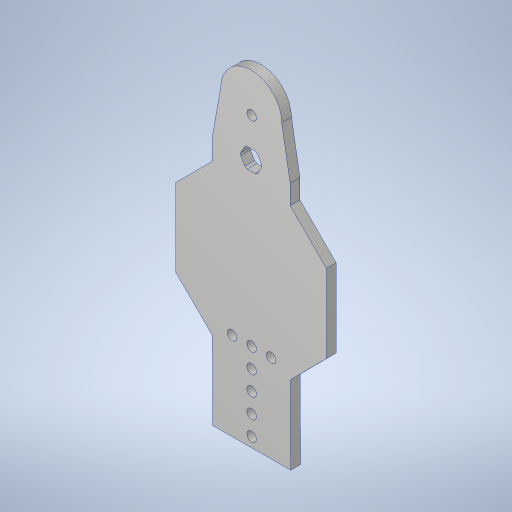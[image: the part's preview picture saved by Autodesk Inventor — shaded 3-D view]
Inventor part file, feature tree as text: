
AUTODESK INVENTOR PART (.ipt)
format: ipt  version: 2023.4 (Build 274418000, 418)  size: 311,808 bytes
history: native  units: in
note: dims shown in document units (in); Inventor stores cm internally (conversion verified against a paired STEP export)
features: extrude x2, sketch x2, hole x1
ambient origin geometry x8: Origin, YZ Plane, XZ Plane, XY Plane, X Axis, Y Axis, Z Axis, Center Point
bodies: Solid1 (feature_tree)
feature tree (5):
  extrude  "Extrusion1"  Depth=2.0in
  sketch  "Sketch2"  dims[d2=1.311in d3=1.311in d4=135.0deg d5=135.0deg d6=2.0in d7=2.0in d8=1.311in d9=1.311in d10=135.0deg d11=135.0deg d12=0.5in d13=0.5in d15=1.25in d16=1.1681in d17=1.25in d18=1.1681in d19=0.25in d20=0.0in d21=0.25in d22=1.0in d23=0.5in d24=0.5in d25=0.5in d26=0.5in d27=0.5in d28=0.5in d29=1.0in d31=1.0in d32=0.25in d33=0.75in d34=0.507in d35=0.25in d36=0.5635in d37=1.0in d38=0.8108in d39=0.25in d40=0.0in d41=0.541in d42=0.5in]
  hole  "Hole1"  [1 undecoded]
  extrude  "Extrusion2"  TaperAngle=135.0deg  [1 undecoded]
  sketch  "Sketch1"  dims[d0=2.0in d1=2.0in]
note: 2 required parameter values undecoded (feature->parameter linkage not recoverable at this tier; creation-order binding heuristic only, values carry confidence <= 0.55)
